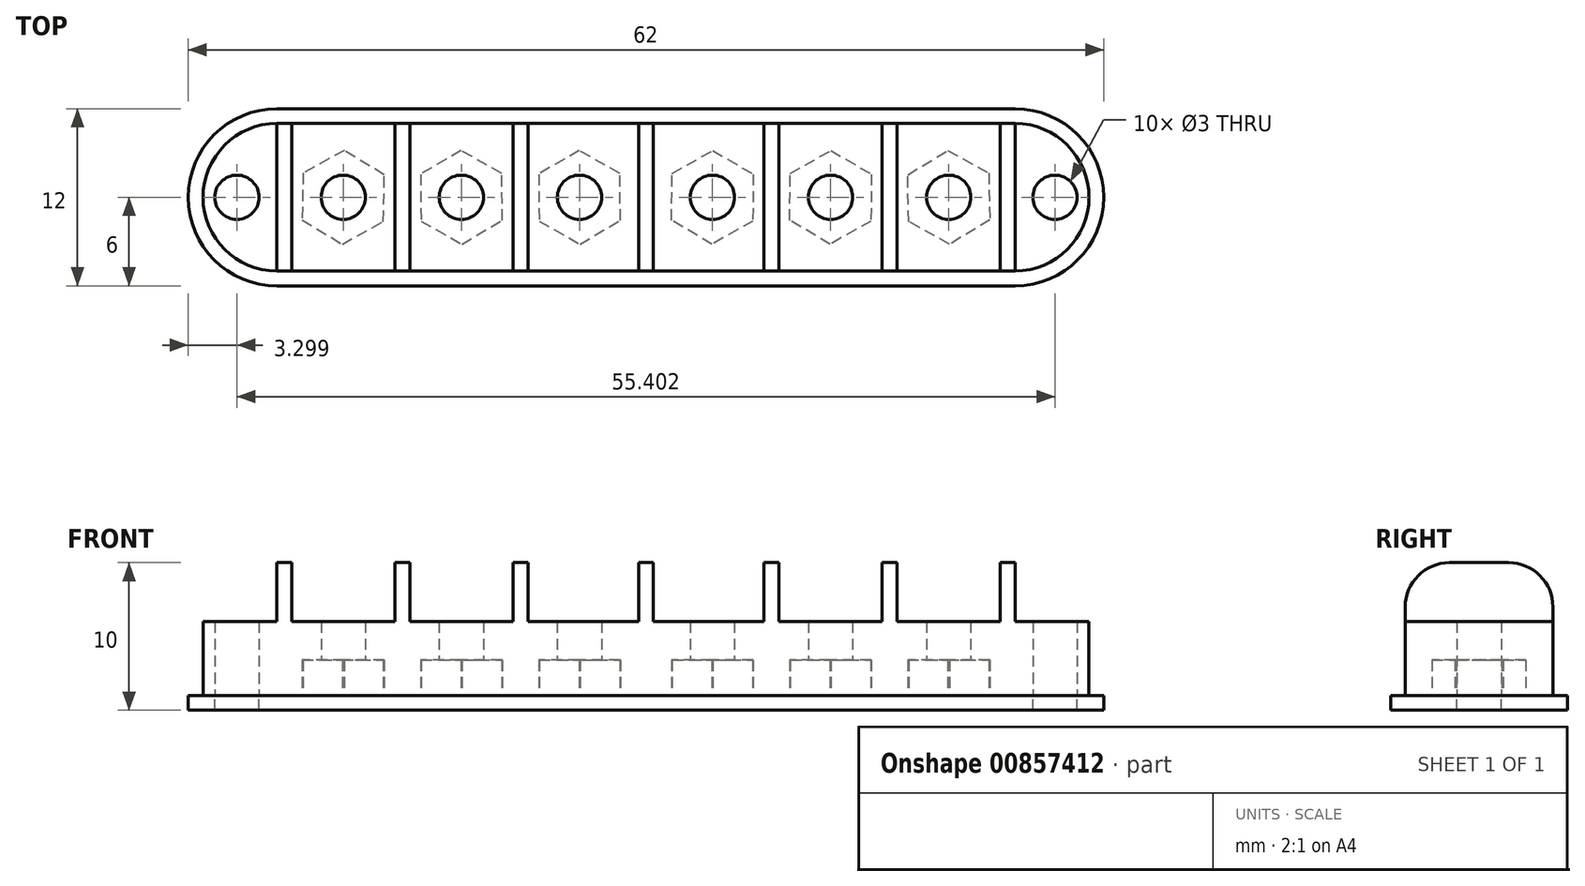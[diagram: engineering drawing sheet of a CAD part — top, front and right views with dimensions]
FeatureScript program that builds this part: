
annotation { "Feature Type Name" : "Feature", "Feature Type Description" : "" }
export const myFeature = defineFeature(function(context is Context, id is Id, definition is map)
    precondition{}
    {
        {
            var Q0;
            Q0=qCreatedBy(makeId("Top.planeOp"),FACE);
            var sketch = newSketch(context, id + "F0", { "sketchPlane" : qUnion([Q0])});
            skLineSegment(sketch, "E0.bottom", {"start": v(25, -5) * mm, "end": v(-25, -5) * mm});
            skLineSegment(sketch, "E0.top", {"start": v(25, 5) * mm, "end": v(-25, 5) * mm});
            skPoint(sketch, "E0.middle", {"position": v(0, 0) * mm});
            skArc(sketch, "E1", {"start": v(-25, 5) * mm, "mid": v(-30, 0) * mm, "end": v(-25, -5) * mm});
            skPoint(sketch, "E2.center.orphan", {"position": v(25, 0) * mm});
            skCircle(sketch, "E3", {"center": v(-27.7, 0) * mm, "radius": 1.5 * mm});
            skArc(sketch, "E4.MirrorCS", {"start": v(25, 5) * mm, "mid": v(30, 0) * mm, "end": v(25, -5) * mm});
            skCircle(sketch, "E5.MirrorC", {"center": v(27.7, 0) * mm, "radius": 1.5 * mm});
            skLineSegment(sketch, "E6", {"start": v(-25, 5) * mm, "end": v(-25, -5) * mm});
            skLineSegment(sketch, "E7", {"start": v(-24, 5) * mm, "end": v(-24, -5) * mm});
            skCircle(sketch, "E8", {"center": v(-20.5, 0) * mm, "radius": 1.5 * mm});
            skLineSegment(sketch, "E9", {"start": v(-17, 5) * mm, "end": v(-17, -5) * mm});
            skLineSegment(sketch, "E10", {"start": v(-16, 5) * mm, "end": v(-16, -5) * mm});
            skCircle(sketch, "E11", {"center": v(-12.5, 0) * mm, "radius": 1.5 * mm});
            skLineSegment(sketch, "E12", {"start": v(-9, 5) * mm, "end": v(-9, -5) * mm});
            skLineSegment(sketch, "E13", {"start": v(-8, 5) * mm, "end": v(-8, -5) * mm});
            skCircle(sketch, "E14", {"center": v(-4.5, 0) * mm, "radius": 1.5 * mm});
            skLineSegment(sketch, "E15", {"start": v(-0.5, 5) * mm, "end": v(-0.5, -5) * mm});
            skLineSegment(sketch, "E16.MirrorCS", {"start": v(25, 5) * mm, "end": v(25, -5) * mm});
            skLineSegment(sketch, "E17.MirrorCS", {"start": v(24, 5) * mm, "end": v(24, -5) * mm});
            skCircle(sketch, "E18.MirrorC", {"center": v(20.5, 0) * mm, "radius": 1.5 * mm});
            skLineSegment(sketch, "E19.MirrorCS", {"start": v(17, 5) * mm, "end": v(17, -5) * mm});
            skLineSegment(sketch, "E20.MirrorCS", {"start": v(16, 5) * mm, "end": v(16, -5) * mm});
            skCircle(sketch, "E21.MirrorC", {"center": v(12.5, 0) * mm, "radius": 1.5 * mm});
            skLineSegment(sketch, "E22.MirrorCS", {"start": v(9, 5) * mm, "end": v(9, -5) * mm});
            skLineSegment(sketch, "E23.MirrorCS", {"start": v(8, 5) * mm, "end": v(8, -5) * mm});
            skCircle(sketch, "E24.MirrorC", {"center": v(4.5, 0) * mm, "radius": 1.5 * mm});
            skLineSegment(sketch, "E25.MirrorCS", {"start": v(0.5, 5) * mm, "end": v(0.5, -5) * mm});
            skSolve(sketch);
        }
        {
            var Q0;
            Q0 = qSketchRegion(id + "F0", true);
            extrude(context, id + "F1", {"entities" : qUnion([Q0]), "depth" : 5 * mm, "offsetDistance" : 25 * mm});
        }
        {
            var Q0;
            {var subQ0=sQuery(id+"F0.wireOp",EDGE,"E6");Q0=makeQuery(id+"F0.imprint","IMPRINT",FACE,{"disambiguationData":[TD([[makeQuery(id+"F0.imprint","IMPRINT",EDGE,{"derivedFrom":subQ0}),1.0]])]});}
            var Q1;
            {var subQ0=sQuery(id+"F0.wireOp",EDGE,"E9");Q1=makeQuery(id+"F0.imprint","IMPRINT",FACE,{"disambiguationData":[TD([[makeQuery(id+"F0.imprint","IMPRINT",EDGE,{"derivedFrom":subQ0}),1.0]])]});}
            var Q2;
            {var subQ0=sQuery(id+"F0.wireOp",EDGE,"E12");Q2=makeQuery(id+"F0.imprint","IMPRINT",FACE,{"disambiguationData":[TD([[makeQuery(id+"F0.imprint","IMPRINT",EDGE,{"derivedFrom":subQ0}),1.0]])]});}
            var Q3;
            {var subQ0=sQuery(id+"F0.wireOp",EDGE,"E15");Q3=makeQuery(id+"F0.imprint","IMPRINT",FACE,{"disambiguationData":[TD([[makeQuery(id+"F0.imprint","IMPRINT",EDGE,{"derivedFrom":subQ0}),1.0]])]});}
            var Q4;
            {var subQ0=sQuery(id+"F0.wireOp",EDGE,"E22.MirrorCS");Q4=makeQuery(id+"F0.imprint","IMPRINT",FACE,{"disambiguationData":[TD([[makeQuery(id+"F0.imprint","IMPRINT",EDGE,{"derivedFrom":subQ0}),-1.0]])]});}
            var Q5;
            {var subQ0=sQuery(id+"F0.wireOp",EDGE,"E19.MirrorCS");Q5=makeQuery(id+"F0.imprint","IMPRINT",FACE,{"disambiguationData":[TD([[makeQuery(id+"F0.imprint","IMPRINT",EDGE,{"derivedFrom":subQ0}),-1.0]])]});}
            var Q6;
            {var subQ0=sQuery(id+"F0.wireOp",EDGE,"E16.MirrorCS");Q6=makeQuery(id+"F0.imprint","IMPRINT",FACE,{"disambiguationData":[TD([[makeQuery(id+"F0.imprint","IMPRINT",EDGE,{"derivedFrom":subQ0}),-1.0]])]});}
            extrude(context, id + "F2", {"entities" : qUnion([Q0, Q1, Q2, Q3, Q4, Q5, Q6]), "operationType" : NewBodyOperationType.ADD, "depth" : 9 * mm, "offsetDistance" : 25 * mm});
        }
        {
            var Q0;
            {var subQ0=sQuery(id+"F0.wireOp",EDGE,"E0.bottom");Q0=makeQuery(id+"F2.opExtrude","CAP_EDGE",EDGE,{"disambiguationData":[OSD([subQ0]),TDD([makeQuery(id+"F0.imprint","IMPRINT",EDGE,{"disambiguationData":[TD([[makeQuery(id+"F0.imprint","INTERSECT",VERTEX,{"derivedFrom":[subQ0,sQuery(id+"F0.wireOp",EDGE,"E7")]}),-1.0]])],"derivedFrom":subQ0})])],"isStart":false});}
            var Q1;
            {var subQ0=sQuery(id+"F0.wireOp",EDGE,"E0.bottom");Q1=makeQuery(id+"F2.opExtrude","CAP_EDGE",EDGE,{"disambiguationData":[OSD([subQ0]),TDD([makeQuery(id+"F0.imprint","IMPRINT",EDGE,{"disambiguationData":[TD([[makeQuery(id+"F0.imprint","INTERSECT",VERTEX,{"derivedFrom":[subQ0,sQuery(id+"F0.wireOp",EDGE,"E9")]}),1.0]])],"derivedFrom":subQ0})])],"isStart":false});}
            var Q2;
            {var subQ0=sQuery(id+"F0.wireOp",EDGE,"E0.bottom");Q2=makeQuery(id+"F2.opExtrude","CAP_EDGE",EDGE,{"disambiguationData":[OSD([subQ0]),TDD([makeQuery(id+"F0.imprint","IMPRINT",EDGE,{"disambiguationData":[TD([[makeQuery(id+"F0.imprint","INTERSECT",VERTEX,{"derivedFrom":[subQ0,sQuery(id+"F0.wireOp",EDGE,"E12")]}),1.0]])],"derivedFrom":subQ0})])],"isStart":false});}
            var Q3;
            {var subQ0=sQuery(id+"F0.wireOp",EDGE,"E0.bottom");Q3=makeQuery(id+"F2.opExtrude","CAP_EDGE",EDGE,{"disambiguationData":[OSD([subQ0]),TDD([makeQuery(id+"F0.imprint","IMPRINT",EDGE,{"disambiguationData":[TD([[makeQuery(id+"F0.imprint","INTERSECT",VERTEX,{"derivedFrom":[subQ0,sQuery(id+"F0.wireOp",EDGE,"E15")]}),1.0]])],"derivedFrom":subQ0})])],"isStart":false});}
            var Q4;
            {var subQ0=sQuery(id+"F0.wireOp",EDGE,"E0.bottom");Q4=makeQuery(id+"F2.opExtrude","CAP_EDGE",EDGE,{"disambiguationData":[OSD([subQ0]),TDD([makeQuery(id+"F0.imprint","IMPRINT",EDGE,{"disambiguationData":[TD([[makeQuery(id+"F0.imprint","INTERSECT",VERTEX,{"derivedFrom":[subQ0,sQuery(id+"F0.wireOp",EDGE,"E22.MirrorCS")]}),-1.0]])],"derivedFrom":subQ0})])],"isStart":false});}
            var Q5;
            {var subQ0=sQuery(id+"F0.wireOp",EDGE,"E0.bottom");Q5=makeQuery(id+"F2.opExtrude","CAP_EDGE",EDGE,{"disambiguationData":[OSD([subQ0]),TDD([makeQuery(id+"F0.imprint","IMPRINT",EDGE,{"disambiguationData":[TD([[makeQuery(id+"F0.imprint","INTERSECT",VERTEX,{"derivedFrom":[subQ0,sQuery(id+"F0.wireOp",EDGE,"E19.MirrorCS")]}),-1.0]])],"derivedFrom":subQ0})])],"isStart":false});}
            var Q6;
            {var subQ0=sQuery(id+"F0.wireOp",EDGE,"E0.bottom");Q6=makeQuery(id+"F2.opExtrude","CAP_EDGE",EDGE,{"disambiguationData":[OSD([subQ0]),TDD([makeQuery(id+"F0.imprint","IMPRINT",EDGE,{"disambiguationData":[TD([[makeQuery(id+"F0.imprint","INTERSECT",VERTEX,{"derivedFrom":[subQ0,sQuery(id+"F0.wireOp",EDGE,"E17.MirrorCS")]}),1.0]])],"derivedFrom":subQ0})])],"isStart":false});}
            var Q7;
            {var subQ0=sQuery(id+"F0.wireOp",EDGE,"E0.top");Q7=makeQuery(id+"F2.opExtrude","CAP_EDGE",EDGE,{"disambiguationData":[OSD([subQ0]),TDD([makeQuery(id+"F0.imprint","IMPRINT",EDGE,{"disambiguationData":[TD([[makeQuery(id+"F0.imprint","INTERSECT",VERTEX,{"derivedFrom":[subQ0,sQuery(id+"F0.wireOp",EDGE,"E17.MirrorCS")]}),1.0]])],"derivedFrom":subQ0})])],"isStart":false});}
            var Q8;
            {var subQ0=sQuery(id+"F0.wireOp",EDGE,"E0.top");Q8=makeQuery(id+"F2.opExtrude","CAP_EDGE",EDGE,{"disambiguationData":[OSD([subQ0]),TDD([makeQuery(id+"F0.imprint","IMPRINT",EDGE,{"disambiguationData":[TD([[makeQuery(id+"F0.imprint","INTERSECT",VERTEX,{"derivedFrom":[subQ0,sQuery(id+"F0.wireOp",EDGE,"E19.MirrorCS")]}),-1.0]])],"derivedFrom":subQ0})])],"isStart":false});}
            var Q9;
            {var subQ0=sQuery(id+"F0.wireOp",EDGE,"E0.top");Q9=makeQuery(id+"F2.opExtrude","CAP_EDGE",EDGE,{"disambiguationData":[OSD([subQ0]),TDD([makeQuery(id+"F0.imprint","IMPRINT",EDGE,{"disambiguationData":[TD([[makeQuery(id+"F0.imprint","INTERSECT",VERTEX,{"derivedFrom":[subQ0,sQuery(id+"F0.wireOp",EDGE,"E22.MirrorCS")]}),-1.0]])],"derivedFrom":subQ0})])],"isStart":false});}
            var Q10;
            {var subQ0=sQuery(id+"F0.wireOp",EDGE,"E0.top");Q10=makeQuery(id+"F2.opExtrude","CAP_EDGE",EDGE,{"disambiguationData":[OSD([subQ0]),TDD([makeQuery(id+"F0.imprint","IMPRINT",EDGE,{"disambiguationData":[TD([[makeQuery(id+"F0.imprint","INTERSECT",VERTEX,{"derivedFrom":[subQ0,sQuery(id+"F0.wireOp",EDGE,"E15")]}),1.0]])],"derivedFrom":subQ0})])],"isStart":false});}
            var Q11;
            {var subQ0=sQuery(id+"F0.wireOp",EDGE,"E0.top");Q11=makeQuery(id+"F2.opExtrude","CAP_EDGE",EDGE,{"disambiguationData":[OSD([subQ0]),TDD([makeQuery(id+"F0.imprint","IMPRINT",EDGE,{"disambiguationData":[TD([[makeQuery(id+"F0.imprint","INTERSECT",VERTEX,{"derivedFrom":[subQ0,sQuery(id+"F0.wireOp",EDGE,"E12")]}),1.0]])],"derivedFrom":subQ0})])],"isStart":false});}
            var Q12;
            {var subQ0=sQuery(id+"F0.wireOp",EDGE,"E0.top");Q12=makeQuery(id+"F2.opExtrude","CAP_EDGE",EDGE,{"disambiguationData":[OSD([subQ0]),TDD([makeQuery(id+"F0.imprint","IMPRINT",EDGE,{"disambiguationData":[TD([[makeQuery(id+"F0.imprint","INTERSECT",VERTEX,{"derivedFrom":[subQ0,sQuery(id+"F0.wireOp",EDGE,"E9")]}),1.0]])],"derivedFrom":subQ0})])],"isStart":false});}
            var Q13;
            {var subQ0=sQuery(id+"F0.wireOp",EDGE,"E0.top");Q13=makeQuery(id+"F2.opExtrude","CAP_EDGE",EDGE,{"disambiguationData":[OSD([subQ0]),TDD([makeQuery(id+"F0.imprint","IMPRINT",EDGE,{"disambiguationData":[TD([[makeQuery(id+"F0.imprint","INTERSECT",VERTEX,{"derivedFrom":[subQ0,sQuery(id+"F0.wireOp",EDGE,"E7")]}),-1.0]])],"derivedFrom":subQ0})])],"isStart":false});}
            fillet(context, id + "F3", {"entities" : qUnion([Q0, Q1, Q2, Q3, Q4, Q5, Q6, Q7, Q8, Q9, Q10, Q11, Q12, Q13]), "radius" : 3 * mm, "tangentPropagation" : true, "allowEdgeOverflow" : false});
        }
        {
            var Q0;
            Q0=makeQuery(id+"F1.opExtrude","CAP_FACE",FACE,{"disambiguationData":[OSD([sQuery(id+"F0.wireOp",EDGE,"E0.bottom"),sQuery(id+"F0.wireOp",EDGE,"E0.top"),sQuery(id+"F0.wireOp",EDGE,"E1"),sQuery(id+"F0.wireOp",EDGE,"E3"),sQuery(id+"F0.wireOp",EDGE,"E4.MirrorCS"),sQuery(id+"F0.wireOp",EDGE,"E5.MirrorC"),sQuery(id+"F0.wireOp",EDGE,"E8"),sQuery(id+"F0.wireOp",EDGE,"E11"),sQuery(id+"F0.wireOp",EDGE,"E14"),sQuery(id+"F0.wireOp",EDGE,"E18.MirrorC"),sQuery(id+"F0.wireOp",EDGE,"E21.MirrorC"),sQuery(id+"F0.wireOp",EDGE,"E24.MirrorC")])],"isStart":true});
            var sketch = newSketch(context, id + "F4", { "sketchPlane" : qUnion([Q0])});
            skCircle(sketch, "E26.cCircle", {"center": v(-20.5, 0) * mm, "radius": 2.75 * mm, "construction": true});
            skLineSegment(sketch, "E26.0", {"start": v(-17.72, -1.53) * mm, "end": v(-20.44, -3.17) * mm});
            skLineSegment(sketch, "E26.1", {"start": v(-20.44, -3.17) * mm, "end": v(-23.22, -1.64) * mm});
            skLineSegment(sketch, "E26.2", {"start": v(-23.22, -1.64) * mm, "end": v(-23.28, 1.53) * mm});
            skLineSegment(sketch, "E26.3", {"start": v(-23.28, 1.53) * mm, "end": v(-20.56, 3.17) * mm});
            skLineSegment(sketch, "E26.4", {"start": v(-20.56, 3.17) * mm, "end": v(-17.78, 1.64) * mm});
            skLineSegment(sketch, "E26.5", {"start": v(-17.78, 1.64) * mm, "end": v(-17.72, -1.53) * mm});
            skPoint(sketch, "E26.0.midPoint", {"position": v(-19.08, -2.35) * mm});
            skCircle(sketch, "E27.cCircle", {"center": v(-12.5, 0) * mm, "radius": 2.75 * mm, "construction": true});
            skLineSegment(sketch, "E27.0", {"start": v(-9.76, -1.61) * mm, "end": v(-12.53, -3.18) * mm});
            skLineSegment(sketch, "E27.1", {"start": v(-12.53, -3.18) * mm, "end": v(-15.26, -1.56) * mm});
            skLineSegment(sketch, "E27.2", {"start": v(-15.26, -1.56) * mm, "end": v(-15.24, 1.61) * mm});
            skLineSegment(sketch, "E27.3", {"start": v(-15.24, 1.61) * mm, "end": v(-12.47, 3.18) * mm});
            skLineSegment(sketch, "E27.4", {"start": v(-12.47, 3.18) * mm, "end": v(-9.74, 1.56) * mm});
            skLineSegment(sketch, "E27.5", {"start": v(-9.74, 1.56) * mm, "end": v(-9.76, -1.61) * mm});
            skPoint(sketch, "E27.0.midPoint", {"position": v(-11.15, -2.4) * mm});
            skCircle(sketch, "E28.cCircle", {"center": v(-4.5, 0) * mm, "radius": 2.75 * mm, "construction": true});
            skLineSegment(sketch, "E28.0", {"start": v(-1.76, -1.61) * mm, "end": v(-4.53, -3.18) * mm});
            skLineSegment(sketch, "E28.1", {"start": v(-4.53, -3.18) * mm, "end": v(-7.26, -1.56) * mm});
            skLineSegment(sketch, "E28.2", {"start": v(-7.26, -1.56) * mm, "end": v(-7.24, 1.61) * mm});
            skLineSegment(sketch, "E28.3", {"start": v(-7.24, 1.61) * mm, "end": v(-4.47, 3.18) * mm});
            skLineSegment(sketch, "E28.4", {"start": v(-4.47, 3.18) * mm, "end": v(-1.74, 1.56) * mm});
            skLineSegment(sketch, "E28.5", {"start": v(-1.74, 1.56) * mm, "end": v(-1.76, -1.61) * mm});
            skPoint(sketch, "E28.0.midPoint", {"position": v(-3.15, -2.4) * mm});
            skCircle(sketch, "E29.MirrorC", {"center": v(20.5, 0) * mm, "radius": 2.75 * mm, "construction": true});
            skLineSegment(sketch, "E30.MirrorCS", {"start": v(23.28, 1.53) * mm, "end": v(20.56, 3.17) * mm});
            skLineSegment(sketch, "E31.MirrorCS", {"start": v(20.56, 3.17) * mm, "end": v(17.78, 1.64) * mm});
            skLineSegment(sketch, "E32.MirrorCS", {"start": v(17.78, 1.64) * mm, "end": v(17.72, -1.53) * mm});
            skLineSegment(sketch, "E33.MirrorCS", {"start": v(17.72, -1.53) * mm, "end": v(20.44, -3.17) * mm});
            skLineSegment(sketch, "E34.MirrorCS", {"start": v(20.44, -3.17) * mm, "end": v(23.22, -1.64) * mm});
            skLineSegment(sketch, "E35.MirrorCS", {"start": v(23.22, -1.64) * mm, "end": v(23.28, 1.53) * mm});
            skLineSegment(sketch, "E36.MirrorCS", {"start": v(15.24, 1.61) * mm, "end": v(12.47, 3.18) * mm});
            skLineSegment(sketch, "E37.MirrorCS", {"start": v(12.47, 3.18) * mm, "end": v(9.74, 1.56) * mm});
            skLineSegment(sketch, "E38.MirrorCS", {"start": v(9.74, 1.56) * mm, "end": v(9.76, -1.61) * mm});
            skLineSegment(sketch, "E39.MirrorCS", {"start": v(9.76, -1.61) * mm, "end": v(12.53, -3.18) * mm});
            skLineSegment(sketch, "E40.MirrorCS", {"start": v(12.53, -3.18) * mm, "end": v(15.26, -1.56) * mm});
            skLineSegment(sketch, "E41.MirrorCS", {"start": v(15.26, -1.56) * mm, "end": v(15.24, 1.61) * mm});
            skLineSegment(sketch, "E42.MirrorCS", {"start": v(7.24, 1.61) * mm, "end": v(4.47, 3.18) * mm});
            skLineSegment(sketch, "E43.MirrorCS", {"start": v(4.47, 3.18) * mm, "end": v(1.74, 1.56) * mm});
            skLineSegment(sketch, "E44.MirrorCS", {"start": v(1.74, 1.56) * mm, "end": v(1.76, -1.61) * mm});
            skLineSegment(sketch, "E45.MirrorCS", {"start": v(1.76, -1.61) * mm, "end": v(4.53, -3.18) * mm});
            skLineSegment(sketch, "E46.MirrorCS", {"start": v(4.53, -3.18) * mm, "end": v(7.26, -1.56) * mm});
            skLineSegment(sketch, "E47.MirrorCS", {"start": v(7.26, -1.56) * mm, "end": v(7.24, 1.61) * mm});
            skSolve(sketch);
        }
        {
            var Q0;
            Q0 = qSketchRegion(id + "F4", true);
            extrude(context, id + "F5", {"entities" : qUnion([Q0]), "operationType" : NewBodyOperationType.REMOVE, "oppositeDirection" : true, "depth" : 2.4 * mm, "offsetDistance" : 25 * mm});
        }
        {
            var Q0;
            Q0=makeQuery(id+"F1.opExtrude","CAP_FACE",FACE,{"disambiguationData":[OSD([sQuery(id+"F0.wireOp",EDGE,"E0.bottom"),sQuery(id+"F0.wireOp",EDGE,"E0.top"),sQuery(id+"F0.wireOp",EDGE,"E1"),sQuery(id+"F0.wireOp",EDGE,"E3"),sQuery(id+"F0.wireOp",EDGE,"E4.MirrorCS"),sQuery(id+"F0.wireOp",EDGE,"E5.MirrorC"),sQuery(id+"F0.wireOp",EDGE,"E8"),sQuery(id+"F0.wireOp",EDGE,"E11"),sQuery(id+"F0.wireOp",EDGE,"E14"),sQuery(id+"F0.wireOp",EDGE,"E18.MirrorC"),sQuery(id+"F0.wireOp",EDGE,"E21.MirrorC"),sQuery(id+"F0.wireOp",EDGE,"E24.MirrorC")])],"isStart":true});
            var sketch = newSketch(context, id + "F6", { "sketchPlane" : qUnion([Q0])});
            skLineSegment(sketch, "E48.0", {"start": v(25, 6) * mm, "end": v(-25, 6) * mm});
            skArc(sketch, "E48.1", {"start": v(25, -6) * mm, "mid": v(31, 0) * mm, "end": v(25, 6) * mm});
            skLineSegment(sketch, "E48.2", {"start": v(25, -6) * mm, "end": v(-25, -6) * mm});
            skArc(sketch, "E48.3", {"start": v(-25, -6) * mm, "mid": v(-31, 0) * mm, "end": v(-25, 6) * mm});
            skCircle(sketch, "E49", {"center": v(-27.7, 0) * mm, "radius": 1.5 * mm});
            skCircle(sketch, "E50", {"center": v(27.7, 0) * mm, "radius": 1.5 * mm});
            skSolve(sketch);
        }
        {
            var Q0;
            Q0 = qSketchRegion(id + "F6", true);
            extrude(context, id + "F7", {"entities" : qUnion([Q0]), "depth" : 1 * mm, "offsetDistance" : 25 * mm});
        }
    });
